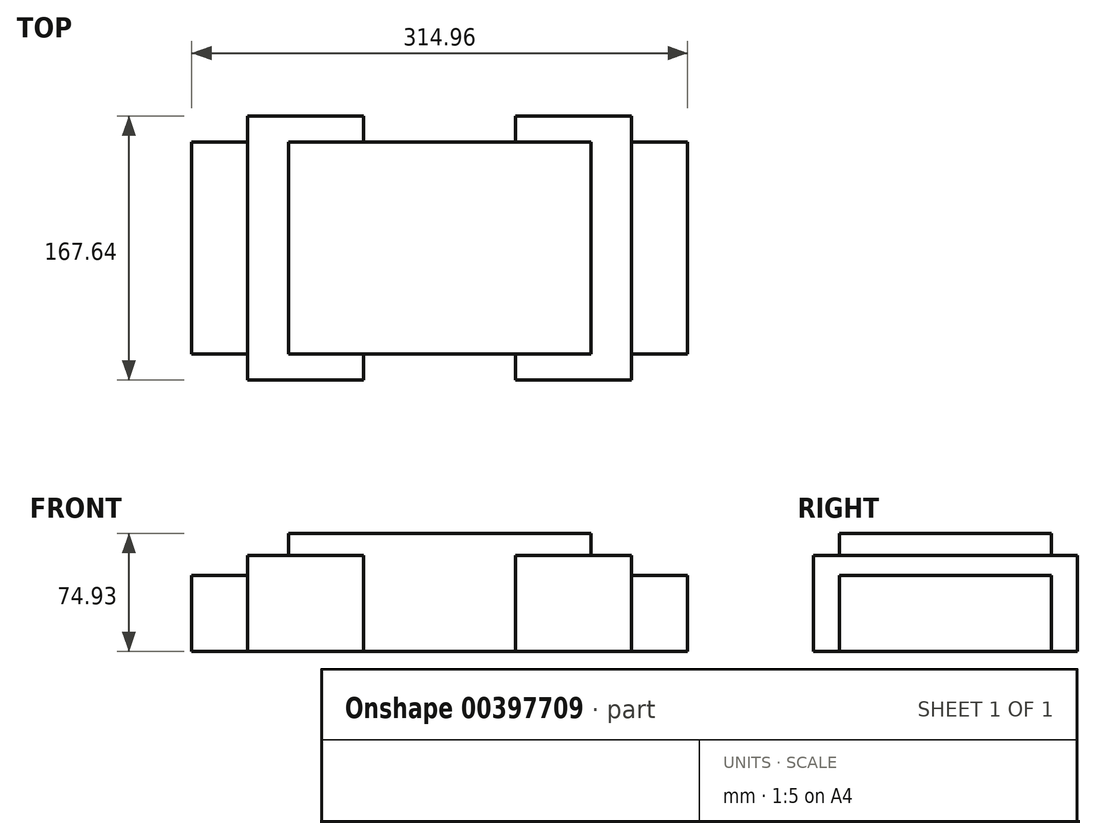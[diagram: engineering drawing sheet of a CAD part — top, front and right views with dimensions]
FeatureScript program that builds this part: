
annotation { "Feature Type Name" : "Feature", "Feature Type Description" : "" }
export const myFeature = defineFeature(function(context is Context, id is Id, definition is map)
    precondition{}
    {
        {
            var Q0;
            Q0=qCreatedBy(makeId("Top.planeOp"),FACE);
            var sketch = newSketch(context, id + "F0", { "sketchPlane" : qUnion([Q0])});
            skLineSegment(sketch, "E0.bottom", {"start": v(0, 0) * mm, "end": v(314.96, 0) * mm});
            skLineSegment(sketch, "E0.top", {"start": v(0, 134.62) * mm, "end": v(314.96, 134.62) * mm});
            skLineSegment(sketch, "E0.left", {"start": v(0, 0) * mm, "end": v(0, 134.62) * mm});
            skLineSegment(sketch, "E0.right", {"start": v(314.96, 0) * mm, "end": v(314.96, 134.62) * mm});
            skLineSegment(sketch, "E1.bottom", {"start": v(0, 134.62) * mm, "end": v(35.56, 134.62) * mm});
            skLineSegment(sketch, "E1.top", {"start": v(0, 149.86) * mm, "end": v(35.56, 149.86) * mm});
            skLineSegment(sketch, "E1.left", {"start": v(0, 134.62) * mm, "end": v(0, 149.86) * mm});
            skLineSegment(sketch, "E1.right", {"start": v(35.56, 134.62) * mm, "end": v(35.56, 149.86) * mm});
            skSolve(sketch);
        }
        {
            var Q0;
            Q0=makeQuery(id+"F0.imprint","IMPRINT",FACE,{"disambiguationData":[TD([[makeQuery(id+"F0.imprint","IMPRINT",EDGE,{"derivedFrom":sQuery(id+"F0.wireOp",EDGE,"E0.bottom")}),1.0]])]});
            extrude(context, id + "F1", {"entities" : qUnion([Q0]), "depth" : 48.26 * mm});
        }
        {
            var Q0;
            Q0=makeQuery(id+"F1.opExtrude","CAP_FACE",FACE,{"disambiguationData":[OSD([sQuery(id+"F0.wireOp",EDGE,"E0.bottom"),sQuery(id+"F0.wireOp",EDGE,"E0.top"),sQuery(id+"F0.wireOp",EDGE,"E0.left"),sQuery(id+"F0.wireOp",EDGE,"E0.right"),sQuery(id+"F0.wireOp",EDGE,"E1.bottom")])],"isStart":false});
            var sketch = newSketch(context, id + "F2", { "sketchPlane" : qUnion([Q0])});
            skLineSegment(sketch, "E2.bottom", {"start": v(0, 134.62) * mm, "end": v(35.56, 134.62) * mm});
            skLineSegment(sketch, "E2.top", {"start": v(0, 149.86) * mm, "end": v(35.56, 149.86) * mm});
            skLineSegment(sketch, "E2.left", {"start": v(0, 134.62) * mm, "end": v(0, 149.86) * mm});
            skLineSegment(sketch, "E2.right", {"start": v(35.56, 134.62) * mm, "end": v(35.56, 149.86) * mm});
            skSolve(sketch);
        }
        {
            var Q0;
            Q0=makeQuery(id+"F2.imprint","IMPRINT",FACE,{"disambiguationData":[TD([[makeQuery(id+"F2.imprint","IMPRINT",EDGE,{"derivedFrom":sQuery(id+"F2.wireOp",EDGE,"E2.bottom")}),1.0]])]});
            extrude(context, id + "F3", {"entities" : qUnion([Q0]), "operationType" : NewBodyOperationType.ADD, "oppositeDirection" : true, "depth" : 25.4 * mm});
        }
        {
            var Q0;
            Q0=makeQuery(id+"F3.opExtrude","SWEPT_FACE",FACE,{"disambiguationData":[OSD([sQuery(id+"F2.wireOp",EDGE,"E2.right")])]});
            extrude(context, id + "F4", {"entities" : qUnion([Q0]), "operationType" : NewBodyOperationType.ADD, "depth" : 73.66 * mm});
        }
        {
            var Q0;
            Q0=makeQuery(id+"F4.opExtrude","CAP_FACE",FACE,{"disambiguationData":[OSD([sQuery(id+"F2.wireOp",EDGE,"E2.right")])],"isStart":false});
            extrude(context, id + "F5", {"entities" : qUnion([Q0]), "operationType" : NewBodyOperationType.REMOVE, "oppositeDirection" : true, "depth" : 152.4 * mm, "hasSecondDirection" : true, "secondDirectionOppositeDirection" : true, "secondDirectionDepth" : 73.66 * mm});
        }
        {
            var Q0;
            {var subQ0=sQuery(id+"F2.wireOp",EDGE,"E2.right");Q0=makeQuery(id+"F4.boolean.opBoolean","MERGE",FACE,{"derivedFrom":[makeQuery(id+"F3.opExtrude","CAP_FACE",FACE,{"disambiguationData":[OSD([sQuery(id+"F2.wireOp",EDGE,"E2.bottom"),sQuery(id+"F2.wireOp",EDGE,"E2.top"),sQuery(id+"F2.wireOp",EDGE,"E2.left"),subQ0])],"isStart":false}),makeQuery(id+"F4.opExtrude","SWEPT_FACE",FACE,{"disambiguationData":[OSD([subQ0]),TDD([makeQuery(id+"F3.opExtrude","CAP_EDGE",EDGE,{"disambiguationData":[OSD([subQ0])],"isStart":false})])]})]});}
            extrude(context, id + "F6", {"entities" : qUnion([Q0]), "operationType" : NewBodyOperationType.ADD, "depth" : 22.86 * mm});
        }
        {
            var Q0;
            {var subQ0=sQuery(id+"F2.wireOp",EDGE,"E2.right");Q0=makeQuery(id+"F6.boolean.opBoolean","MERGE",FACE,{"derivedFrom":[makeQuery(id+"F4.opExtrude","CAP_FACE",FACE,{"disambiguationData":[OSD([subQ0])],"isStart":false}),makeQuery(id+"F6.opExtrude","SWEPT_FACE",FACE,{"disambiguationData":[OSD([subQ0]),TDD([makeQuery(id+"F4.opExtrude","CAP_EDGE",EDGE,{"disambiguationData":[OSD([subQ0]),TDD([makeQuery(id+"F3.opExtrude","CAP_EDGE",EDGE,{"disambiguationData":[OSD([subQ0])],"isStart":false})])],"isStart":false})])]})]});}
            extrude(context, id + "F7", {"entities" : qUnion([Q0]), "operationType" : NewBodyOperationType.ADD, "depth" : 170.18 * mm, "hasSecondDirection" : true, "secondDirectionOppositeDirection" : false, "secondDirectionDepth" : 96.52 * mm});
        }
        {
            var Q0;
            Q0=makeQuery(id+"F1.opExtrude","SWEPT_BODY",BODY,{"disambiguationData":[OSD([sQuery(id+"F0.wireOp",EDGE,"E0.bottom"),sQuery(id+"F0.wireOp",EDGE,"E0.top"),sQuery(id+"F0.wireOp",EDGE,"E0.left"),sQuery(id+"F0.wireOp",EDGE,"E0.right"),sQuery(id+"F0.wireOp",EDGE,"E1.bottom")])]});
            deleteBodies(context, id + "F8", {"entities" : qUnion([Q0])});
        }
        {
            var Q0;
            Q0=qCreatedBy(makeId("Top.planeOp"),FACE);
            var sketch = newSketch(context, id + "F9", { "sketchPlane" : qUnion([Q0])});
            skLineSegment(sketch, "E3.bottom", {"start": v(0, 0) * mm, "end": v(157.48, 0) * mm});
            skLineSegment(sketch, "E3.top", {"start": v(0, 67.31) * mm, "end": v(157.48, 67.31) * mm});
            skLineSegment(sketch, "E3.left", {"start": v(0, 0) * mm, "end": v(0, 67.31) * mm});
            skLineSegment(sketch, "E3.right", {"start": v(157.48, 0) * mm, "end": v(157.48, 67.31) * mm});
            skSolve(sketch);
        }
        {
            var Q0;
            Q0=makeQuery(id+"F9.imprint","IMPRINT",FACE,{"disambiguationData":[TD([[makeQuery(id+"F9.imprint","IMPRINT",EDGE,{"derivedFrom":sQuery(id+"F9.wireOp",EDGE,"E3.bottom")}),1.0]])]});
            extrude(context, id + "F10", {"entities" : qUnion([Q0]), "depth" : 48.26 * mm});
        }
        {
            var Q0;
            Q0=makeQuery(id+"F10.opExtrude","SWEPT_FACE",FACE,{"disambiguationData":[OSD([sQuery(id+"F9.wireOp",EDGE,"E3.top")])]});
            var sketch = newSketch(context, id + "F11", { "sketchPlane" : qUnion([Q0])});
            skLineSegment(sketch, "E4.bottom", {"start": v(-157.48, 0) * mm, "end": v(-121.92, 0) * mm});
            skLineSegment(sketch, "E4.top", {"start": v(-157.48, 48.26) * mm, "end": v(-121.92, 48.26) * mm});
            skLineSegment(sketch, "E4.left", {"start": v(-157.48, 0) * mm, "end": v(-157.48, 48.26) * mm});
            skLineSegment(sketch, "E4.right", {"start": v(-121.92, 0) * mm, "end": v(-121.92, 48.26) * mm});
            skSolve(sketch);
        }
        {
            var Q0;
            Q0=makeQuery(id+"F11.imprint","IMPRINT",FACE,{"disambiguationData":[TD([[makeQuery(id+"F11.imprint","IMPRINT",EDGE,{"derivedFrom":sQuery(id+"F11.wireOp",EDGE,"E4.bottom")}),-1.0]])]});
            extrude(context, id + "F12", {"entities" : qUnion([Q0]), "operationType" : NewBodyOperationType.ADD, "depth" : 16.5 * mm});
        }
        {
            var Q0;
            Q0=makeQuery(id+"F12.opExtrude","SWEPT_FACE",FACE,{"disambiguationData":[OSD([sQuery(id+"F11.wireOp",EDGE,"E4.right")])]});
            extrude(context, id + "F13", {"entities" : qUnion([Q0]), "operationType" : NewBodyOperationType.ADD, "depth" : 73.66 * mm});
        }
        {
            var Q0;
            Q0=makeQuery(id+"F13.opExtrude","CAP_FACE",FACE,{"disambiguationData":[OSD([sQuery(id+"F11.wireOp",EDGE,"E4.right")])],"isStart":false});
            extrude(context, id + "F14", {"entities" : qUnion([Q0]), "operationType" : NewBodyOperationType.REMOVE, "oppositeDirection" : true, "depth" : 152.4 * mm, "hasSecondDirection" : true, "secondDirectionOppositeDirection" : true, "secondDirectionDepth" : 73.66 * mm});
        }
        {
            var Q0;
            Q0=makeQuery(id+"F10.opExtrude","SWEPT_BODY",BODY,{"disambiguationData":[OSD([sQuery(id+"F9.wireOp",EDGE,"E3.bottom"),sQuery(id+"F9.wireOp",EDGE,"E3.top"),sQuery(id+"F9.wireOp",EDGE,"E3.left"),sQuery(id+"F9.wireOp",EDGE,"E3.right")])]});
            var Q1;
            Q1=qCreatedBy(makeId("Front.planeOp"),FACE);
            mirror(context, id + "F15", {"operationType" : NewBodyOperationType.ADD, "entities" : qUnion([Q0]), "mirrorPlane" : qUnion([Q1])});
        }
        {
            var Q0;
            Q0=makeQuery(id+"F10.opExtrude","SWEPT_BODY",BODY,{"disambiguationData":[OSD([sQuery(id+"F9.wireOp",EDGE,"E3.bottom"),sQuery(id+"F9.wireOp",EDGE,"E3.top"),sQuery(id+"F9.wireOp",EDGE,"E3.left"),sQuery(id+"F9.wireOp",EDGE,"E3.right")])]});
            var Q1;
            Q1=qCreatedBy(makeId("Right.planeOp"),FACE);
            mirror(context, id + "F16", {"operationType" : NewBodyOperationType.ADD, "entities" : qUnion([Q0]), "mirrorPlane" : qUnion([Q1])});
        }
        {
            var Q0;
            {var subQ0=sQuery(id+"F11.wireOp",EDGE,"E4.top");var subQ1=sQuery(id+"F9.wireOp",EDGE,"E3.top");var subQ2=makeQuery(id+"F13.boolean.opBoolean","MERGE",FACE,{"derivedFrom":[makeQuery(id+"F12.boolean.opBoolean","MERGE",FACE,{"derivedFrom":[makeQuery(id+"F10.opExtrude","CAP_FACE",FACE,{"disambiguationData":[OSD([sQuery(id+"F9.wireOp",EDGE,"E3.bottom"),subQ1,sQuery(id+"F9.wireOp",EDGE,"E3.left"),sQuery(id+"F9.wireOp",EDGE,"E3.right")])],"isStart":false}),makeQuery(id+"F12.opExtrude","SWEPT_FACE",FACE,{"disambiguationData":[OSD([subQ0])]})]}),makeQuery(id+"F13.opExtrude","SWEPT_FACE",FACE,{"disambiguationData":[OSD([subQ1,subQ0,sQuery(id+"F11.wireOp",EDGE,"E4.right")])]})]});var subQ3=makeQuery(id+"F15.boolean.opBoolean","MERGE",FACE,{"derivedFrom":[subQ2,makeQuery(id+"F15.opPattern","COPY",FACE,{"derivedFrom":subQ2,"instanceName":"1"})]});Q0=makeQuery(id+"F16.boolean.opBoolean","MERGE",FACE,{"derivedFrom":[subQ3,makeQuery(id+"F16.opPattern","COPY",FACE,{"derivedFrom":subQ3,"instanceName":"1"})]});}
            var sketch = newSketch(context, id + "F17", { "sketchPlane" : qUnion([Q0])});
            skLineSegment(sketch, "E5.bottom", {"start": v(-157.48, 67.31) * mm, "end": v(-121.92, 67.31) * mm});
            skLineSegment(sketch, "E5.top", {"start": v(-157.48, -67.31) * mm, "end": v(-121.92, -67.31) * mm});
            skLineSegment(sketch, "E5.left", {"start": v(-157.48, 67.31) * mm, "end": v(-157.48, -67.31) * mm});
            skLineSegment(sketch, "E5.right", {"start": v(-121.92, 67.31) * mm, "end": v(-121.92, -67.31) * mm});
            skSolve(sketch);
        }
        {
            var Q0;
            Q0=makeQuery(id+"F17.imprint","IMPRINT",FACE,{"disambiguationData":[TD([[makeQuery(id+"F17.imprint","IMPRINT",EDGE,{"derivedFrom":sQuery(id+"F17.wireOp",EDGE,"E5.right")}),1.0]])]});
            extrude(context, id + "F18", {"entities" : qUnion([Q0]), "operationType" : NewBodyOperationType.ADD, "depth" : 12.7 * mm});
        }
        {
            var Q0;
            Q0=makeQuery(id+"F18.opExtrude","CAP_FACE",FACE,{"disambiguationData":[OSD([sQuery(id+"F9.wireOp",EDGE,"E3.top"),sQuery(id+"F9.wireOp",EDGE,"E3.right"),sQuery(id+"F11.wireOp",EDGE,"E4.top"),sQuery(id+"F11.wireOp",EDGE,"E4.left"),sQuery(id+"F11.wireOp",EDGE,"E4.right"),sQuery(id+"F17.wireOp",EDGE,"E5.right")])],"isStart":false});
            var sketch = newSketch(context, id + "F19", { "sketchPlane" : qUnion([Q0])});
            skLineSegment(sketch, "E6.bottom", {"start": v(121.92, -67.31) * mm, "end": v(157.48, -67.31) * mm});
            skLineSegment(sketch, "E6.top", {"start": v(121.92, 67.31) * mm, "end": v(157.48, 67.31) * mm});
            skLineSegment(sketch, "E6.left", {"start": v(121.92, -67.31) * mm, "end": v(121.92, 67.31) * mm});
            skLineSegment(sketch, "E6.right", {"start": v(157.48, -67.31) * mm, "end": v(157.48, 67.31) * mm});
            skSolve(sketch);
        }
        {
            var Q0;
            Q0=makeQuery(id+"F19.imprint","IMPRINT",FACE,{"disambiguationData":[TD([[makeQuery(id+"F19.imprint","IMPRINT",EDGE,{"derivedFrom":sQuery(id+"F19.wireOp",EDGE,"E6.bottom")}),-1.0]])]});
            extrude(context, id + "F20", {"entities" : qUnion([Q0]), "operationType" : NewBodyOperationType.REMOVE, "oppositeDirection" : true, "depth" : 12.7 * mm});
        }
        {
            var Q0;
            Q0=makeQuery(id+"F18.opExtrude","CAP_FACE",FACE,{"disambiguationData":[OSD([sQuery(id+"F9.wireOp",EDGE,"E3.top"),sQuery(id+"F9.wireOp",EDGE,"E3.right"),sQuery(id+"F11.wireOp",EDGE,"E4.top"),sQuery(id+"F11.wireOp",EDGE,"E4.left"),sQuery(id+"F11.wireOp",EDGE,"E4.right"),sQuery(id+"F17.wireOp",EDGE,"E5.right")])],"isStart":false});
            var sketch = newSketch(context, id + "F21", { "sketchPlane" : qUnion([Q0])});
            skLineSegment(sketch, "E7.bottom", {"start": v(0, 67.31) * mm, "end": v(95.9, 67.31) * mm});
            skLineSegment(sketch, "E7.top", {"start": v(0, 0) * mm, "end": v(95.9, 0) * mm});
            skLineSegment(sketch, "E7.left", {"start": v(0, 67.31) * mm, "end": v(0, 0) * mm});
            skLineSegment(sketch, "E7.right", {"start": v(95.9, 67.31) * mm, "end": v(95.9, 0) * mm});
            skSolve(sketch);
        }
        {
            var Q0;
            Q0=makeQuery(id+"F21.imprint","IMPRINT",FACE,{"disambiguationData":[TD([[makeQuery(id+"F21.imprint","IMPRINT",EDGE,{"derivedFrom":sQuery(id+"F21.wireOp",EDGE,"E7.top")}),1.0]])]});
            extrude(context, id + "F22", {"entities" : qUnion([Q0]), "operationType" : NewBodyOperationType.ADD, "depth" : 13.97 * mm});
        }
        {
            var Q0;
            Q0=makeQuery(id+"F10.opExtrude","SWEPT_BODY",BODY,{"disambiguationData":[OSD([sQuery(id+"F9.wireOp",EDGE,"E3.bottom"),sQuery(id+"F9.wireOp",EDGE,"E3.top"),sQuery(id+"F9.wireOp",EDGE,"E3.left"),sQuery(id+"F9.wireOp",EDGE,"E3.right")])]});
            var Q1;
            Q1=qCreatedBy(makeId("Front.planeOp"),FACE);
            mirror(context, id + "F23", {"operationType" : NewBodyOperationType.ADD, "entities" : qUnion([Q0]), "mirrorPlane" : qUnion([Q1])});
        }
        {
            var Q0;
            Q0=makeQuery(id+"F10.opExtrude","SWEPT_BODY",BODY,{"disambiguationData":[OSD([sQuery(id+"F9.wireOp",EDGE,"E3.bottom"),sQuery(id+"F9.wireOp",EDGE,"E3.top"),sQuery(id+"F9.wireOp",EDGE,"E3.left"),sQuery(id+"F9.wireOp",EDGE,"E3.right")])]});
            var Q1;
            Q1=qCreatedBy(makeId("Right.planeOp"),FACE);
            mirror(context, id + "F24", {"operationType" : NewBodyOperationType.ADD, "entities" : qUnion([Q0]), "mirrorPlane" : qUnion([Q1])});
        }
    });
